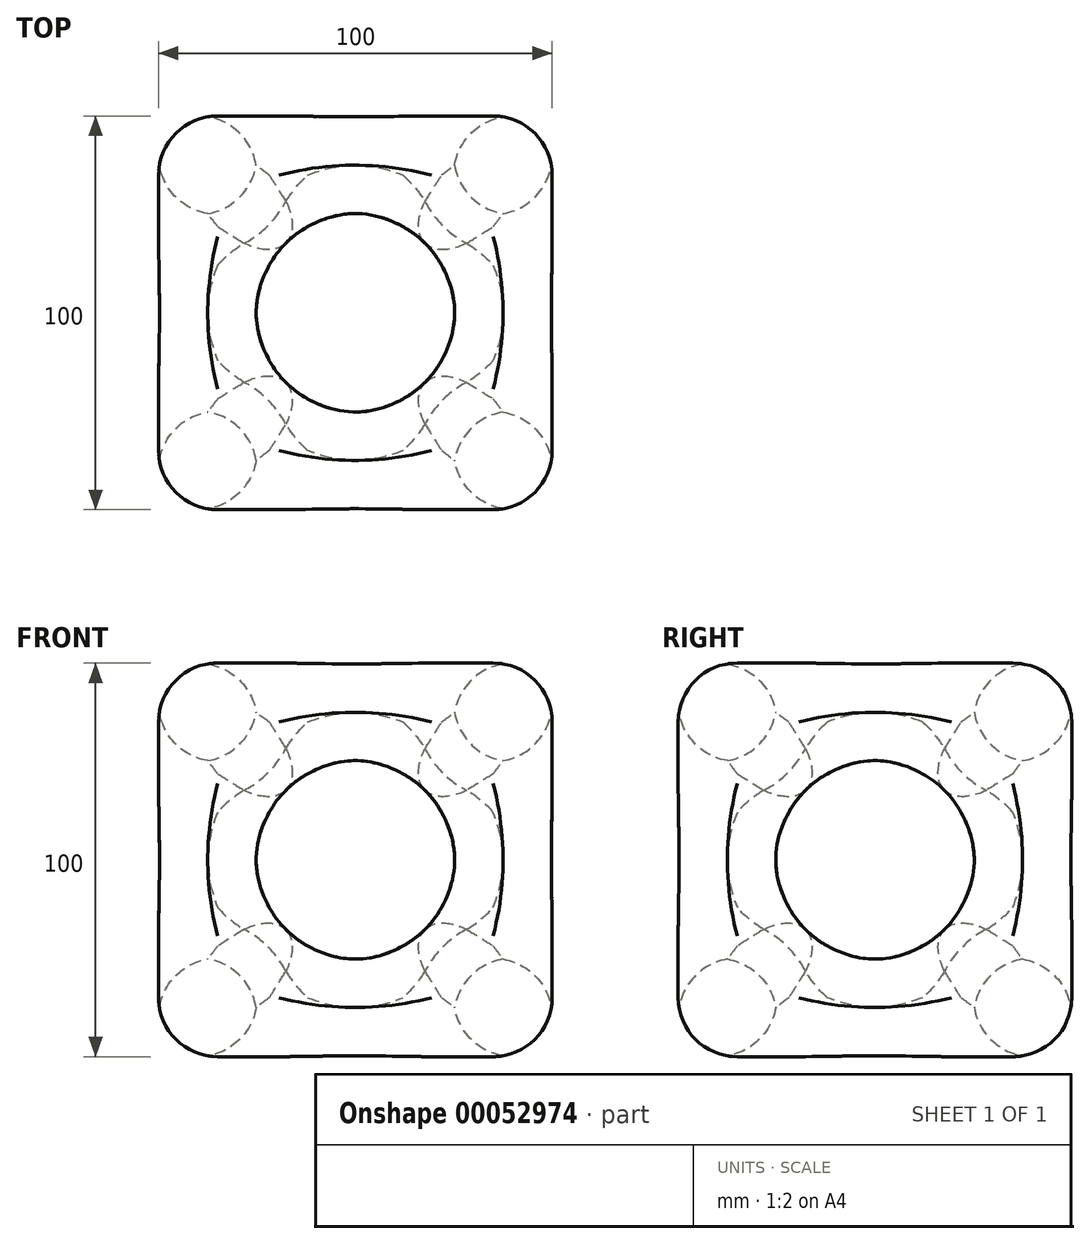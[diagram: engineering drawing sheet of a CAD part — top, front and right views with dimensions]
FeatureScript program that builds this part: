
annotation { "Feature Type Name" : "Feature", "Feature Type Description" : "" }
export const myFeature = defineFeature(function(context is Context, id is Id, definition is map)
    precondition{}
    {
        {
            var Q0;
            Q0=qCreatedBy(makeId("Top.planeOp"),FACE);
            var sketch = newSketch(context, id + "F0", { "sketchPlane" : qUnion([Q0])});
            skLineSegment(sketch, "E0.rect.bottom", {"start": v(-50, -50) * mm, "end": v(50, -50) * mm});
            skLineSegment(sketch, "E0.rect.top", {"start": v(-50, 50) * mm, "end": v(50, 50) * mm});
            skLineSegment(sketch, "E0.rect.left", {"start": v(-50, -50) * mm, "end": v(-50, 50) * mm});
            skLineSegment(sketch, "E0.rect.right", {"start": v(50, -50) * mm, "end": v(50, 50) * mm});
            skPoint(sketch, "E0.rect.middle", {"position": v(0, 0) * mm});
            skSolve(sketch);
        }
        {
            var Q0;
            Q0 = qSketchRegion(id + "F0", true);
            extrude(context, id + "F1", {"entities" : qUnion([Q0]), "depth" : 100 * mm});
        }
        {
            var Q0;
            Q0=makeQuery(id+"F1.opExtrude","CAP_FACE",FACE,{"disambiguationData":[OSD([sQuery(id+"F0.wireOp",EDGE,"E0.rect.bottom"),sQuery(id+"F0.wireOp",EDGE,"E0.rect.top"),sQuery(id+"F0.wireOp",EDGE,"E0.rect.left"),sQuery(id+"F0.wireOp",EDGE,"E0.rect.right")])],"isStart":false});
            var sketch = newSketch(context, id + "F2", { "sketchPlane" : qUnion([Q0])});
            skCircle(sketch, "E1", {"center": v(0, 0) * mm, "radius": 25 * mm});
            skSolve(sketch);
        }
        {
            var Q0;
            Q0=makeQuery(id+"F2.imprint","IMPRINT",FACE,{"disambiguationData":[TD([[makeQuery(id+"F2.imprint","IMPRINT",EDGE,{"derivedFrom":sQuery(id+"F2.wireOp",EDGE,"E1")}),1.0]])]});
            extrude(context, id + "F3", {"entities" : qUnion([Q0]), "operationType" : NewBodyOperationType.REMOVE, "oppositeDirection" : true, "depth" : 102.23 * mm});
        }
        {
            var Q0;
            Q0=makeQuery(id+"F1.opExtrude","SWEPT_FACE",FACE,{"disambiguationData":[OSD([sQuery(id+"F0.wireOp",EDGE,"E0.rect.top")])]});
            var sketch = newSketch(context, id + "F4", { "sketchPlane" : qUnion([Q0])});
            skCircle(sketch, "E2", {"center": v(0, 50) * mm, "radius": 25 * mm});
            skPoint(sketch, "E2.centerSnap0", {"position": v(50, 50) * mm});
            skPoint(sketch, "E2.centerSnap1", {"position": v(0, 0) * mm});
            skSolve(sketch);
        }
        {
            var Q0;
            Q0=makeQuery(id+"F4.imprint","IMPRINT",FACE,{"disambiguationData":[TD([[makeQuery(id+"F4.imprint","IMPRINT",EDGE,{"derivedFrom":sQuery(id+"F4.wireOp",EDGE,"E2")}),1.0]])]});
            extrude(context, id + "F5", {"entities" : qUnion([Q0]), "operationType" : NewBodyOperationType.REMOVE, "oppositeDirection" : true, "depth" : 144.82 * mm});
        }
        {
            var Q0;
            Q0=makeQuery(id+"F1.opExtrude","SWEPT_FACE",FACE,{"disambiguationData":[OSD([sQuery(id+"F0.wireOp",EDGE,"E0.rect.right")])]});
            var sketch = newSketch(context, id + "F6", { "sketchPlane" : qUnion([Q0])});
            skCircle(sketch, "E3", {"center": v(0, 50) * mm, "radius": 25 * mm});
            skPoint(sketch, "E3.centerSnap0", {"position": v(50, 50) * mm});
            skSolve(sketch);
        }
        {
            var Q0;
            Q0 = qSketchRegion(id + "F6", true);
            extrude(context, id + "F7", {"entities" : qUnion([Q0]), "operationType" : NewBodyOperationType.REMOVE, "oppositeDirection" : true, "depth" : 247.72 * mm});
        }
        {
            var Q0;
            Q0=makeQuery(id+"F1.opExtrude","SWEPT_FACE",FACE,{"disambiguationData":[OSD([sQuery(id+"F0.wireOp",EDGE,"E0.rect.bottom")])]});
            var Q1;
            Q1=makeQuery(id+"F1.opExtrude","CAP_FACE",FACE,{"disambiguationData":[OSD([sQuery(id+"F0.wireOp",EDGE,"E0.rect.bottom"),sQuery(id+"F0.wireOp",EDGE,"E0.rect.top"),sQuery(id+"F0.wireOp",EDGE,"E0.rect.left"),sQuery(id+"F0.wireOp",EDGE,"E0.rect.right")])],"isStart":false});
            var Q2;
            Q2=makeQuery(id+"F1.opExtrude","SWEPT_FACE",FACE,{"disambiguationData":[OSD([sQuery(id+"F0.wireOp",EDGE,"E0.rect.left")])]});
            var Q3;
            Q3=makeQuery(id+"F1.opExtrude","CAP_FACE",FACE,{"disambiguationData":[OSD([sQuery(id+"F0.wireOp",EDGE,"E0.rect.bottom"),sQuery(id+"F0.wireOp",EDGE,"E0.rect.top"),sQuery(id+"F0.wireOp",EDGE,"E0.rect.left"),sQuery(id+"F0.wireOp",EDGE,"E0.rect.right")])],"isStart":true});
            var Q4;
            Q4=makeQuery(id+"F1.opExtrude","SWEPT_FACE",FACE,{"disambiguationData":[OSD([sQuery(id+"F0.wireOp",EDGE,"E0.rect.right")])]});
            var Q5;
            Q5=makeQuery(id+"F1.opExtrude","SWEPT_FACE",FACE,{"disambiguationData":[OSD([sQuery(id+"F0.wireOp",EDGE,"E0.rect.top")])]});
            fillet(context, id + "F8", {"entities" : qUnion([Q0, Q1, Q2, Q3, Q4, Q5]), "radius" : 15 * mm, "tangentPropagation" : true, "allowEdgeOverflow" : false});
        }
        {
            var Q0;
            {var subQ0=makeQuery(id+"F3.boolean.opBoolean","COPY",FACE,{"derivedFrom":makeQuery(id+"F3.opExtrude","SWEPT_FACE",FACE,{"disambiguationData":[OSD([sQuery(id+"F2.wireOp",EDGE,"E1")])]})});Q0=makeQuery(id+"F5.boolean.opBoolean","SPLIT",FACE,{"disambiguationData":[TD([makeQuery(id+"F1.opExtrude","CAP_FACE",FACE,{"disambiguationData":[OSD([sQuery(id+"F0.wireOp",EDGE,"E0.rect.bottom"),sQuery(id+"F0.wireOp",EDGE,"E0.rect.top"),sQuery(id+"F0.wireOp",EDGE,"E0.rect.left"),sQuery(id+"F0.wireOp",EDGE,"E0.rect.right")])],"isStart":false})])],"derivedFrom":subQ0});}
            var Q1;
            Q1=makeQuery(id+"F7.boolean.opBoolean","COPY",FACE,{"disambiguationData":[OD(1.0)],"derivedFrom":makeQuery(id+"F7.opExtrude","SWEPT_FACE",FACE,{"disambiguationData":[OSD([sQuery(id+"F6.wireOp",EDGE,"E3")])]})});
            var Q2;
            Q2=makeQuery(id+"F5.boolean.opBoolean","COPY",FACE,{"disambiguationData":[OD(0.0)],"derivedFrom":makeQuery(id+"F5.opExtrude","SWEPT_FACE",FACE,{"disambiguationData":[OSD([sQuery(id+"F4.wireOp",EDGE,"E2")])]})});
            var Q3;
            Q3=makeQuery(id+"F7.boolean.opBoolean","COPY",FACE,{"disambiguationData":[OD(0.0)],"derivedFrom":makeQuery(id+"F7.opExtrude","SWEPT_FACE",FACE,{"disambiguationData":[OSD([sQuery(id+"F6.wireOp",EDGE,"E3")])]})});
            var Q4;
            Q4=makeQuery(id+"F5.boolean.opBoolean","COPY",FACE,{"disambiguationData":[OD(1.0)],"derivedFrom":makeQuery(id+"F5.opExtrude","SWEPT_FACE",FACE,{"disambiguationData":[OSD([sQuery(id+"F4.wireOp",EDGE,"E2")])]})});
            fillet(context, id + "F9", {"entities" : qUnion([Q0, Q1, Q2, Q3, Q4]), "radius" : 15 * mm, "tangentPropagation" : true, "allowEdgeOverflow" : false});
        }
    });
